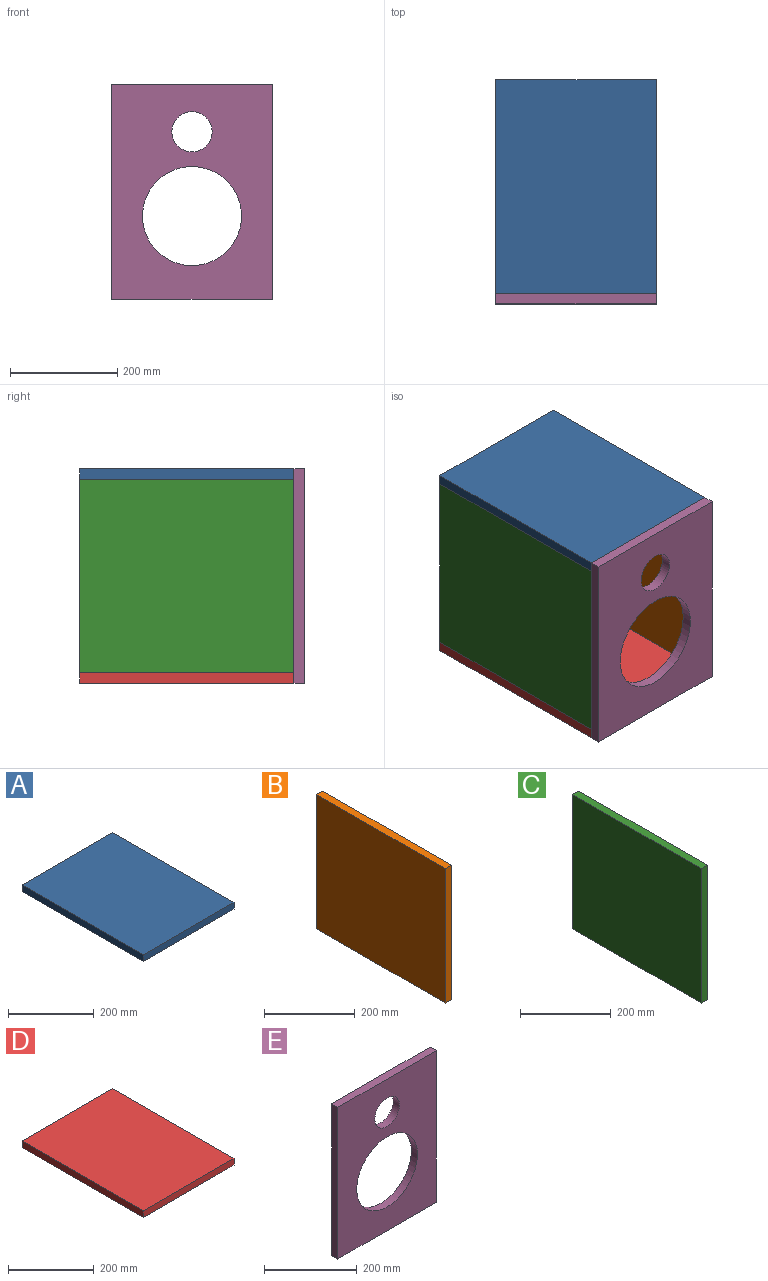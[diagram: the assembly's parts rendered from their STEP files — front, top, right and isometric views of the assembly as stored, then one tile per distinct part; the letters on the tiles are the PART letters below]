
ASSEMBLY  parts=5 mates=4
PART A: 6 faces, bbox 300x400x19 mm
  f0: plane 300x19mm, normal (0,1,0), area 5700mm2, adj f1,f3,f4,f5
  f1: plane 400x19mm, normal (-1,0,0), area 7600mm2, adj f0,f2,f4,f5
  f2: plane 300x19mm, normal (0,-1,0), area 5700mm2, adj f1,f3,f4,f5
  f3: plane 400x19mm, normal (1,0,0), area 7600mm2, adj f0,f2,f4,f5
  f4: plane 400x300mm, normal (0,0,1), area 120000mm2, adj f0,f1,f2,f3
  f5: plane 400x300mm, normal (0,0,-1), area 120000mm2, adj f0,f1,f2,f3
PART B: 6 faces, bbox 19x400x362 mm
  f0: plane 362x19mm, normal (0,-1,0), area 6878mm2, adj f1,f3,f4,f5
  f1: plane 400x19mm, normal (0,0,-1), area 7600mm2, adj f0,f2,f4,f5
  f2: plane 362x19mm, normal (0,1,0), area 6878mm2, adj f1,f3,f4,f5
  f3: plane 400x19mm, normal (0,0,1), area 7600mm2, adj f0,f2,f4,f5
  f4: plane 400x362mm, normal (1,0,0), area 144800mm2, adj f0,f1,f2,f3
  f5: plane 400x362mm, normal (-1,0,0), area 144800mm2, adj f0,f1,f2,f3
PART C: 6 faces, bbox 19x400x362 mm
  f0: plane 362x19mm, normal (0,-1,0), area 6878mm2, adj f1,f3,f4,f5
  f1: plane 400x19mm, normal (0,0,-1), area 7600mm2, adj f0,f2,f4,f5
  f2: plane 362x19mm, normal (0,1,0), area 6878mm2, adj f1,f3,f4,f5
  f3: plane 400x19mm, normal (0,0,1), area 7600mm2, adj f0,f2,f4,f5
  f4: plane 400x362mm, normal (1,0,0), area 144800mm2, adj f0,f1,f2,f3
  f5: plane 400x362mm, normal (-1,0,0), area 144800mm2, adj f0,f1,f2,f3
PART D: 6 faces, bbox 300x400x19 mm
  f0: plane 300x19mm, normal (0,1,0), area 5700mm2, adj f1,f3,f4,f5
  f1: plane 400x19mm, normal (-1,0,0), area 7600mm2, adj f0,f2,f4,f5
  f2: plane 300x19mm, normal (0,-1,0), area 5700mm2, adj f1,f3,f4,f5
  f3: plane 400x19mm, normal (1,0,0), area 7600mm2, adj f0,f2,f4,f5
  f4: plane 400x300mm, normal (0,0,1), area 120000mm2, adj f0,f1,f2,f3
  f5: plane 400x300mm, normal (0,0,-1), area 120000mm2, adj f0,f1,f2,f3
PART E: 8 faces, bbox 300x19x400 mm
  f0: plane 400x19mm, normal (-1,0,0), area 7600mm2, adj f1,f3,f4,f5
  f1: plane 300x19mm, normal (0,0,-1), area 5700mm2, adj f0,f2,f4,f5
  f2: plane 400x19mm, normal (1,0,0), area 7600mm2, adj f1,f3,f4,f5
  f3: plane 300x19mm, normal (0,0,1), area 5700mm2, adj f0,f2,f4,f5
  f4: plane 400x300mm, normal (0,-1,0), area 88701.9mm2, adj f0,f1,f2,f3,f6,f7
  f5: plane 400x300mm, normal (0,1,0), area 88701.9mm2, adj f0,f1,f2,f3,f6,f7
  f6: cylinder r=92.5mm len=185mm, axis (0,-1,0), area 11042.7mm2, adj f4,f5
  f7: cylinder r=37.5mm len=75mm, axis (0,-1,0), area 4476.8mm2, adj f4,f5
PLACE A t=(-100.14,247.3,281.42)mm
PLACE B t=(53,199.48,103.11)mm
PLACE C t=(-228,219.73,83.75)mm
PLACE D t=(-73.42,205.9,-99.58)mm
PLACE E t=(-114,39.11,81.7)mm
MATE fastened E.f5 <-> C.f0  axis (0,1,0) through (-228,39.11,100.42)mm
MATE fastened E.f5 <-> A.f2  axis (0,1,0) through (-78,39.11,300.42)mm
MATE fastened E.f5 <-> B.f0  axis (0,1,0) through (72,39.11,100.42)mm
MATE fastened E.f5 <-> D.f2  axis (0,1,0) through (-78,39.11,-99.58)mm
